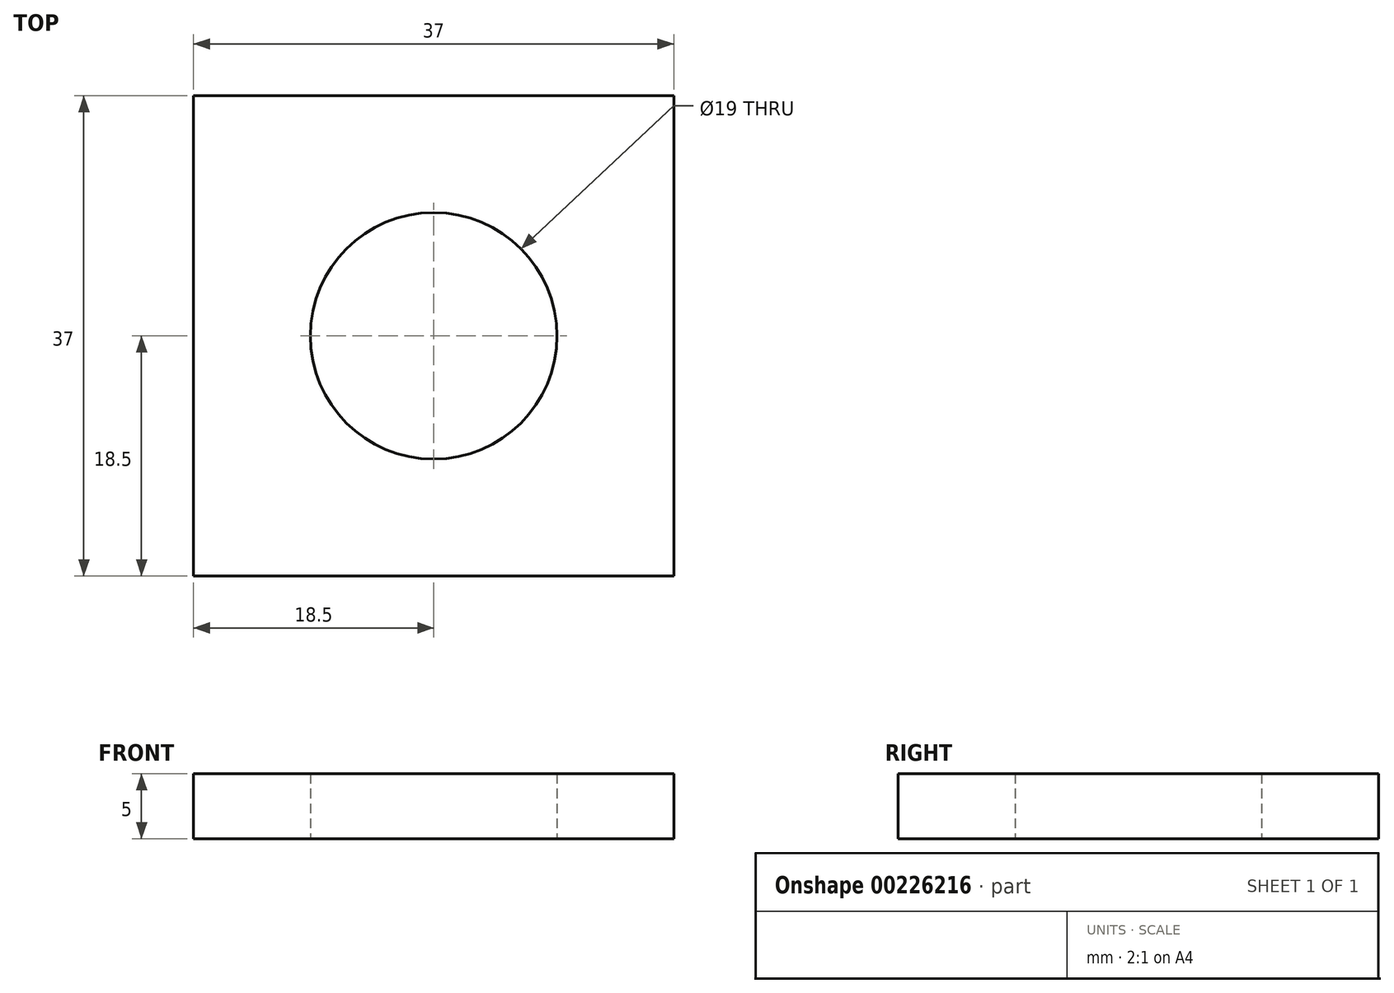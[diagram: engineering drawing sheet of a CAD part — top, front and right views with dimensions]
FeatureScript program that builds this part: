
annotation { "Feature Type Name" : "Feature", "Feature Type Description" : "" }
export const myFeature = defineFeature(function(context is Context, id is Id, definition is map)
    precondition{}
    {
        {
            var Q0;
            Q0=qCreatedBy(makeId("Front.planeOp"),FACE);
            var sketch = newSketch(context, id + "F0", { "sketchPlane" : qUnion([Q0])});
            skCircle(sketch, "E0", {"center": v(0, 0) * mm, "radius": 9.5 * mm});
            skLineSegment(sketch, "E1.bottom", {"start": v(18.5, 18.5) * mm, "end": v(-18.5, 18.5) * mm});
            skLineSegment(sketch, "E1.top", {"start": v(18.5, -18.5) * mm, "end": v(-18.5, -18.5) * mm});
            skLineSegment(sketch, "E1.left", {"start": v(18.5, 18.5) * mm, "end": v(18.5, -18.5) * mm});
            skLineSegment(sketch, "E1.right", {"start": v(-18.5, 18.5) * mm, "end": v(-18.5, -18.5) * mm});
            skSolve(sketch);
        }
        {
            var Q0;
            Q0=makeQuery(id+"F0.imprint","IMPRINT",FACE,{"disambiguationData":[TD([[makeQuery(id+"F0.imprint","IMPRINT",EDGE,{"derivedFrom":sQuery(id+"F0.wireOp",EDGE,"E0")}),-1.0]])]});
            extrude(context, id + "F1", {"entities" : qUnion([Q0]), "depth" : 5 * mm});
        }
        {
            var Q0;
            Q0=makeQuery(id+"F1.opExtrude","SWEPT_BODY",BODY,{"disambiguationData":[OSD([sQuery(id+"F0.wireOp",EDGE,"E0"),sQuery(id+"F0.wireOp",EDGE,"E1.bottom"),sQuery(id+"F0.wireOp",EDGE,"E1.top"),sQuery(id+"F0.wireOp",EDGE,"E1.left"),sQuery(id+"F0.wireOp",EDGE,"E1.right")])]});
            var Q1;
            Q1=qCreatedBy(makeId("Origin.pointOp"),VERTEX);
            var Q2;
            Q2=makeQuery(id+"F1.opExtrude","CAP_EDGE",EDGE,{"disambiguationData":[OSD([sQuery(id+"F0.wireOp",EDGE,"E1.bottom")])],"isStart":true});
            transform(context, id + "F2", {"entities" : qUnion([Q0]), "transformType" : TransformType.ROTATION, "transformAxis" : qUnion([Q2]), "angle" : 90 * degree, "makeCopy" : false});
        }
        {
            var Q0;
            Q0=makeQuery(id+"F1.opExtrude","SWEPT_BODY",BODY,{"disambiguationData":[OSD([sQuery(id+"F0.wireOp",EDGE,"E0"),sQuery(id+"F0.wireOp",EDGE,"E1.bottom"),sQuery(id+"F0.wireOp",EDGE,"E1.top"),sQuery(id+"F0.wireOp",EDGE,"E1.left"),sQuery(id+"F0.wireOp",EDGE,"E1.right")])]});
            transform(context, id + "F3", {"entities" : qUnion([Q0]), "transformType" : TransformType.TRANSLATION_3D, "dx" : 16 * mm, "dy" : 32 * mm, "dz" : -21 * mm, "makeCopy" : false});
        }
    });
